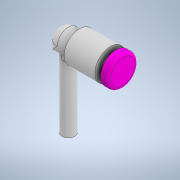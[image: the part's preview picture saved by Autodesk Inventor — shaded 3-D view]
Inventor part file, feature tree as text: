
AUTODESK INVENTOR PART (.ipt)
format: ipt  version: 2021 (Build 250183000, 183)  size: 173,568 bytes
history: native  units: mm
features: extrude x6, sketch x5, fillet x2, plane x1, projected_geometry x1
ambient origin geometry x8: Origin, YZ Plane, XZ Plane, XY Plane, X Axis, Y Axis, Z Axis, Center Point
bodies: Solid1 (feature_tree)
feature tree (15):
  extrude  "Extrusion1"  Depth=25.0mm TaperAngle=0.0deg
  extrude  "Extrusion2"  Depth=17.0mm TaperAngle=0.0deg
  sketch  "Sketch3"  dims[d6=7.0mm d7=3.5mm d8=0.0mm]
  extrude  "Extrusion3"  Depth=3.5mm TaperAngle=0.0deg
  extrude  "Extrusion4"  Depth=3.5mm
  extrude  "Extrusion5"  Depth=3.5mm
  fillet  "Fillet1"  [1 undecoded]
  plane  "Work Plane1"
  extrude  "Extrusion6"  Depth=1.0mm
  fillet  "Fillet2"  Radius=1.8mm
  sketch  "Sketch1"  dims[d0=4.0mm d1=25.0mm d2=0.0mm]
  sketch  "Sketch2"  dims[d3=9.6mm d4=17.0mm d5=0.0mm]
  sketch  "Sketch4"  dims[d9=3.5mm d10=0.0mm d11=7.0mm]
  projected_geometry  "Projected Loop1"
  sketch  "Sketch5"  dims[d12=0.0mm d13=0.0mm d14=3.5mm d15=-3.0mm d16=5.5mm d17=1.8mm d18=0.0mm d19=1.0mm]
note: 1 required parameter value undecoded (feature->parameter linkage not recoverable at this tier; creation-order binding heuristic only, values carry confidence <= 0.55)
